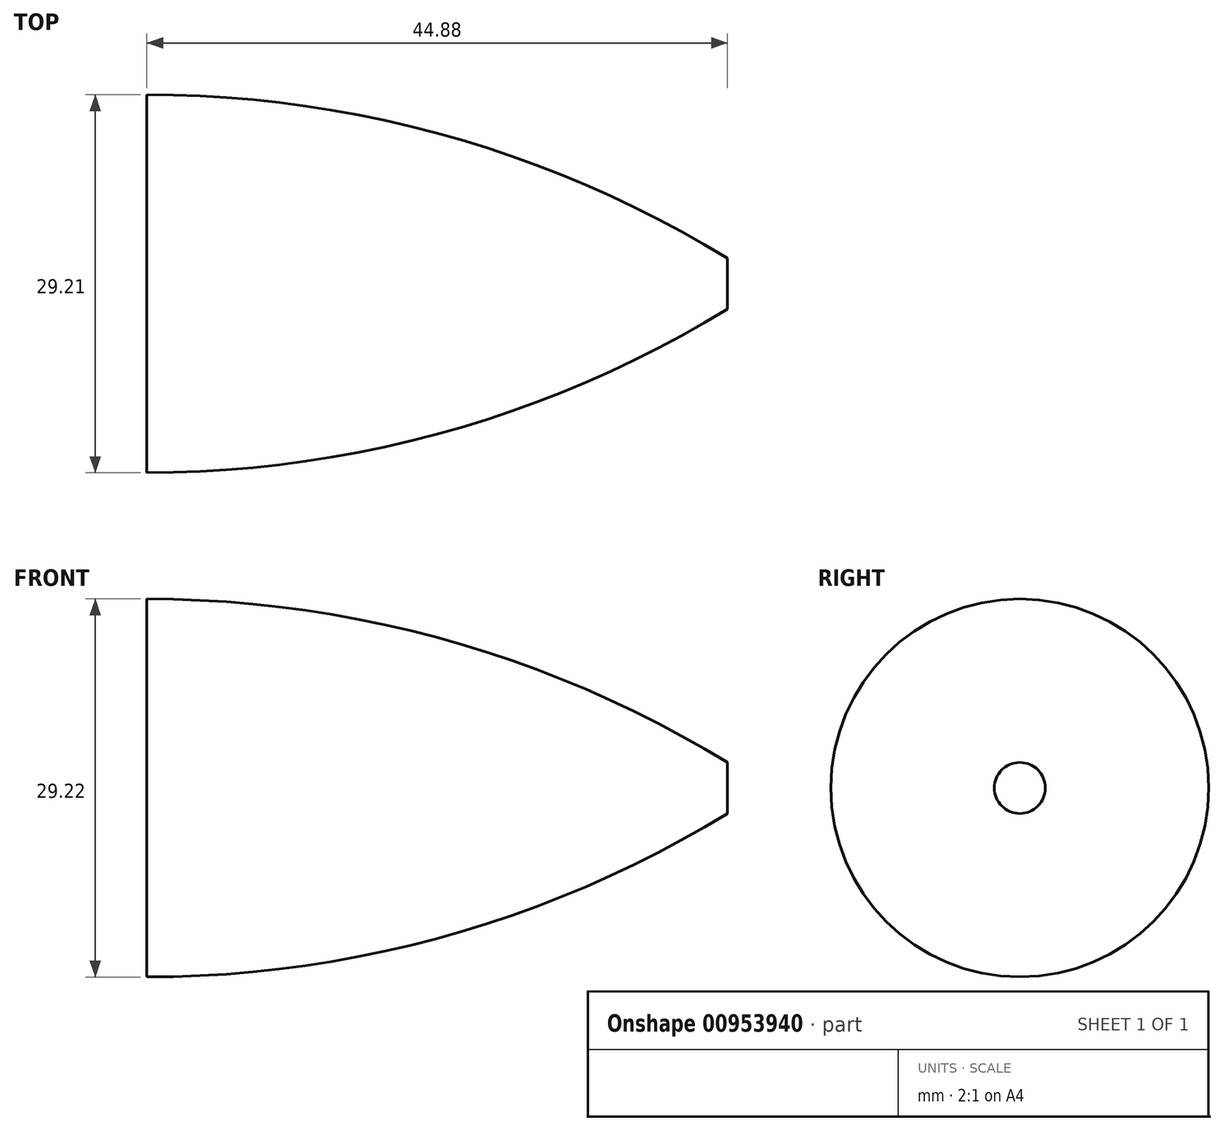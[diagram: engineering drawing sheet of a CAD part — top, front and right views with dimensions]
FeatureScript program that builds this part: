
annotation { "Feature Type Name" : "Feature", "Feature Type Description" : "" }
export const myFeature = defineFeature(function(context is Context, id is Id, definition is map)
    precondition{}
    {
        {
            var Q0;
            Q0=qCreatedBy(makeId("Top.planeOp"),FACE);
            var sketch = newSketch(context, id + "F0", { "sketchPlane" : qUnion([Q0])});
            skLineSegment(sketch, "E0.bottom", {"start": v(43.2, 2.35) * mm, "end": v(88.08, 2.35) * mm, "construction": true});
            skLineSegment(sketch, "E0.top", {"start": v(43.2, -26.86) * mm, "end": v(88.08, -26.86) * mm, "construction": true});
            skLineSegment(sketch, "E0.left", {"start": v(43.2, 2.35) * mm, "end": v(43.2, -26.86) * mm, "construction": true});
            skLineSegment(sketch, "E0.right", {"start": v(88.08, 2.35) * mm, "end": v(88.08, -26.86) * mm, "construction": true});
            skLineSegment(sketch, "E1", {"start": v(39.11, -12.25) * mm, "end": v(97.6, -12.25) * mm});
            skLineSegment(sketch, "E2", {"start": v(88.08, -10.28) * mm, "end": v(88.08, -12.25) * mm});
            skLineSegment(sketch, "E3", {"start": v(43.2, -12.25) * mm, "end": v(43.2, 2.35) * mm});
            skArc(sketch, "E4", {"start": v(88.08, -10.28) * mm, "mid": v(66.51, -0.87) * mm, "end": v(43.2, 2.35) * mm});
            skLineSegment(sketch, "E5", {"start": v(43.2, -12.25) * mm, "end": v(88.08, -12.25) * mm});
            skSolve(sketch);
        }
        {
            var Q0;
            {var subQ2=sQuery(id+"F0.wireOp",EDGE,"E2");Q0=makeQuery(id+"F0.imprint","IMPRINT",FACE,{"disambiguationData":[TD([[makeQuery(id+"F0.imprint","IMPRINT",EDGE,{"derivedFrom":subQ2}),-1.0]])]});}
            var Q1;
            Q1=sQuery(id+"F0.wireOp",EDGE,"E1");
            revolve(context, id + "F1", {"surfaceOperationType" : NewSurfaceOperationType.NEW, "entities" : qUnion([Q0]), "axis" : qUnion([Q1]), "revolveType" : RevolveType.FULL});
        }
    });
